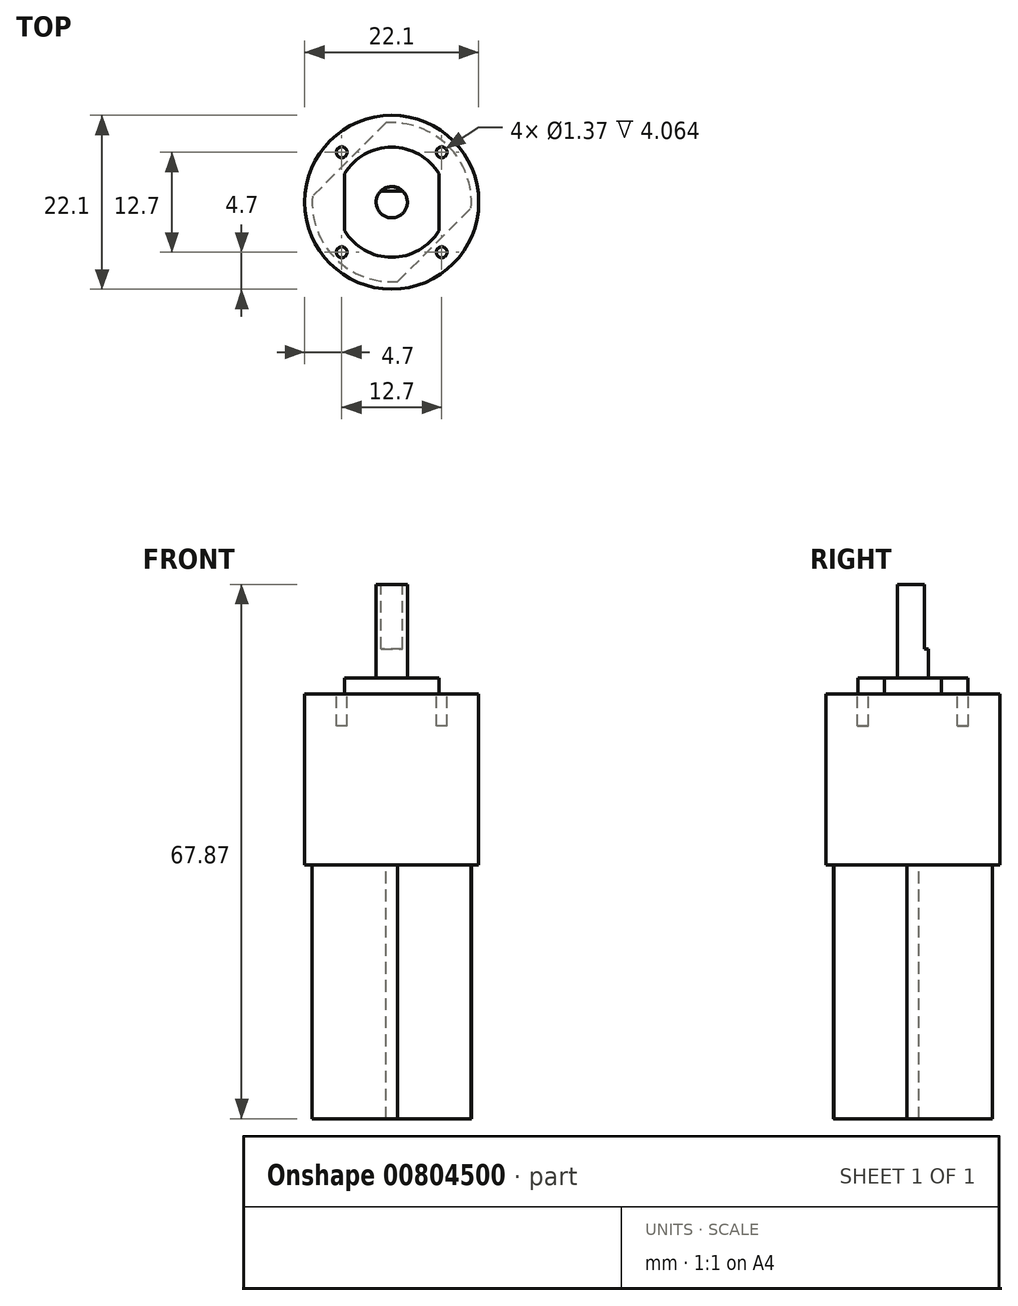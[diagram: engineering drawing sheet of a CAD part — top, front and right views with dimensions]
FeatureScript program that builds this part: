
annotation { "Feature Type Name" : "Feature", "Feature Type Description" : "" }
export const myFeature = defineFeature(function(context is Context, id is Id, definition is map)
    precondition{}
    {
        {
            var Q0;
            Q0=qCreatedBy(makeId("Top.planeOp"),FACE);
            var sketch = newSketch(context, id + "F0", { "sketchPlane" : qUnion([Q0])});
            skCircle(sketch, "E0", {"center": v(0, 0) * mm, "radius": 11.05 * mm});
            skSolve(sketch);
        }
        {
            var Q0;
            Q0 = qSketchRegion(id + "F0", true);
            extrude(context, id + "F1", {"entities" : qUnion([Q0]), "depth" : 21.72 * mm, "offsetDistance" : 25.4 * mm});
        }
        {
            var Q0;
            Q0=makeQuery(id+"F1.opExtrude","CAP_FACE",FACE,{"disambiguationData":[OSD([sQuery(id+"F0.wireOp",EDGE,"E0")])],"isStart":false});
            var sketch = newSketch(context, id + "F2", { "sketchPlane" : qUnion([Q0])});
            skCircle(sketch, "E1", {"center": v(0, 0) * mm, "radius": 7 * mm});
            skLineSegment(sketch, "E2.bottom", {"start": v(6, 3.61) * mm, "end": v(-6, 3.61) * mm, "construction": true});
            skLineSegment(sketch, "E2.top", {"start": v(6, -3.61) * mm, "end": v(-6, -3.61) * mm, "construction": true});
            skLineSegment(sketch, "E2.left", {"start": v(6, 3.61) * mm, "end": v(6, -3.61) * mm});
            skLineSegment(sketch, "E2.right", {"start": v(-6, 3.61) * mm, "end": v(-6, -3.61) * mm});
            skSolve(sketch);
        }
        {
            var Q0;
            {var subQ0=sQuery(id+"F2.wireOp",EDGE,"E2.left");Q0=makeQuery(id+"F2.imprint","IMPRINT",FACE,{"disambiguationData":[TD([[makeQuery(id+"F2.imprint","IMPRINT",EDGE,{"derivedFrom":subQ0}),-1.0]])]});}
            extrude(context, id + "F3", {"entities" : qUnion([Q0]), "operationType" : NewBodyOperationType.ADD, "depth" : 2.08 * mm, "offsetDistance" : 25.4 * mm});
        }
        {
            var Q0;
            Q0=makeQuery(id+"F3.opExtrude","CAP_FACE",FACE,{"disambiguationData":[OSD([sQuery(id+"F2.wireOp",EDGE,"E1"),sQuery(id+"F2.wireOp",EDGE,"E2.left"),sQuery(id+"F2.wireOp",EDGE,"E2.right")])],"isStart":false});
            var sketch = newSketch(context, id + "F4", { "sketchPlane" : qUnion([Q0])});
            skCircle(sketch, "E3", {"center": v(0, 0) * mm, "radius": 1.98 * mm});
            skSolve(sketch);
        }
        {
            var Q0;
            Q0 = qSketchRegion(id + "F4", true);
            extrude(context, id + "F5", {"entities" : qUnion([Q0]), "operationType" : NewBodyOperationType.ADD, "depth" : 11.86 * mm, "offsetDistance" : 25.4 * mm});
        }
        {
            var Q0;
            Q0=makeQuery(id+"F5.opExtrude","CAP_FACE",FACE,{"disambiguationData":[OSD([sQuery(id+"F4.wireOp",EDGE,"E3")])],"isStart":false});
            var sketch = newSketch(context, id + "F6", { "sketchPlane" : qUnion([Q0])});
            skLineSegment(sketch, "E4", {"start": v(-1.38, 1.42) * mm, "end": v(1.38, 1.42) * mm});
            skCircle(sketch, "E5.0.0", {"center": v(0, 0) * mm, "radius": 1.98 * mm});
            skSolve(sketch);
        }
        {
            var Q0;
            {var subQ0=sQuery(id+"F6.wireOp",EDGE,"E4");Q0=makeQuery(id+"F6.imprint","IMPRINT",FACE,{"disambiguationData":[TD([[makeQuery(id+"F6.imprint","IMPRINT",EDGE,{"derivedFrom":subQ0}),1.0]])]});}
            extrude(context, id + "F7", {"entities" : qUnion([Q0]), "operationType" : NewBodyOperationType.REMOVE, "oppositeDirection" : true, "depth" : 8.18 * mm, "offsetDistance" : 25.4 * mm});
        }
        {
            var Q0;
            Q0=makeQuery(id+"F1.opExtrude","CAP_FACE",FACE,{"disambiguationData":[OSD([sQuery(id+"F0.wireOp",EDGE,"E0")])],"isStart":false});
            var sketch = newSketch(context, id + "F8", { "sketchPlane" : qUnion([Q0])});
            skLineSegment(sketch, "E6.bottom", {"start": v(6.35, -6.35) * mm, "end": v(-6.35, -6.35) * mm, "construction": true});
            skLineSegment(sketch, "E6.top", {"start": v(6.35, 6.35) * mm, "end": v(-6.35, 6.35) * mm, "construction": true});
            skLineSegment(sketch, "E6.left", {"start": v(6.35, -6.35) * mm, "end": v(6.35, 6.35) * mm, "construction": true});
            skLineSegment(sketch, "E6.right", {"start": v(-6.35, -6.35) * mm, "end": v(-6.35, 6.35) * mm, "construction": true});
            skPoint(sketch, "E6.middle", {"position": v(0, 0) * mm});
            skCircle(sketch, "E7", {"center": v(-6.35, 6.35) * mm, "radius": 0.69 * mm});
            skCircle(sketch, "E8", {"center": v(6.35, 6.35) * mm, "radius": 0.69 * mm});
            skCircle(sketch, "E9", {"center": v(6.35, -6.35) * mm, "radius": 0.69 * mm});
            skCircle(sketch, "E10", {"center": v(-6.35, -6.35) * mm, "radius": 0.69 * mm});
            skSolve(sketch);
        }
        {
            var Q0;
            Q0 = qSketchRegion(id + "F8", true);
            extrude(context, id + "F9", {"entities" : qUnion([Q0]), "operationType" : NewBodyOperationType.REMOVE, "oppositeDirection" : true, "depth" : 4.06 * mm, "offsetDistance" : 25.4 * mm});
        }
        {
            var Q0;
            Q0=makeQuery(id+"F1.opExtrude","CAP_FACE",FACE,{"disambiguationData":[OSD([sQuery(id+"F0.wireOp",EDGE,"E0")])],"isStart":true});
            var sketch = newSketch(context, id + "F10", { "sketchPlane" : qUnion([Q0])});
            skCircle(sketch, "E11", {"center": v(0, 0) * mm, "radius": 10.1 * mm});
            skLineSegment(sketch, "E12", {"start": v(0.75, 10.08) * mm, "end": v(10.08, 0.75) * mm});
            skLineSegment(sketch, "E13", {"start": v(-0.75, -10.08) * mm, "end": v(-10.08, -0.75) * mm});
            skLineSegment(sketch, "E14", {"start": v(5.42, 5.42) * mm, "end": v(-5.42, -5.42) * mm, "construction": true});
            skLineSegment(sketch, "E15", {"start": v(0, 0) * mm, "end": v(10.1, 0) * mm, "construction": true});
            skSolve(sketch);
        }
        {
            var Q0;
            {var subQ0=sQuery(id+"F10.wireOp",EDGE,"E12");Q0=makeQuery(id+"F10.imprint","IMPRINT",FACE,{"disambiguationData":[TD([[makeQuery(id+"F10.imprint","IMPRINT",EDGE,{"derivedFrom":subQ0}),-1.0]])]});}
            extrude(context, id + "F11", {"entities" : qUnion([Q0]), "operationType" : NewBodyOperationType.ADD, "depth" : 32.2 * mm, "offsetDistance" : 25.4 * mm});
        }
    });
